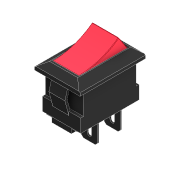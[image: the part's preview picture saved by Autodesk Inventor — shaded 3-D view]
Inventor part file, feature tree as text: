
AUTODESK INVENTOR PART (.ipt)
format: ipt  version: 2021 (Build 250183000, 183)  size: 327,680 bytes
history: native  units: mm
features: other x20, sketch x1, fillet x1
ambient origin geometry x8: Origin, YZ Plane, XZ Plane, XY Plane, X Axis, Y Axis, Z Axis, Center Point
bodies: Body1 (feature_tree), Body2 (feature_tree)
feature tree (22):
  other  "Твердое тело1"
  sketch  "Эскиз1"
  other  "Непосредственное редактирование1"
  other  "Непосредственное редактирование2"
  other  "Непосредственное редактирование3"
  other  "Непосредственное редактирование4"
  other  "Непосредственное редактирование5"
  other  "Непосредственное редактирование6"
  other  "Твердое тело2"
  other  "LPattern1"
  fillet  "Fillet1"  Radius=0.15mm
  other  "Размер1"
  other  "Размер2"
  other  "Размер3"
  other  "Размер4"
  other  "Размер5"
  other  "Размер6"
  other  "Размер7"
  other  "Размер8"
  other  "Размер9"
  other  "Размер10"
  other  "Размер11"
